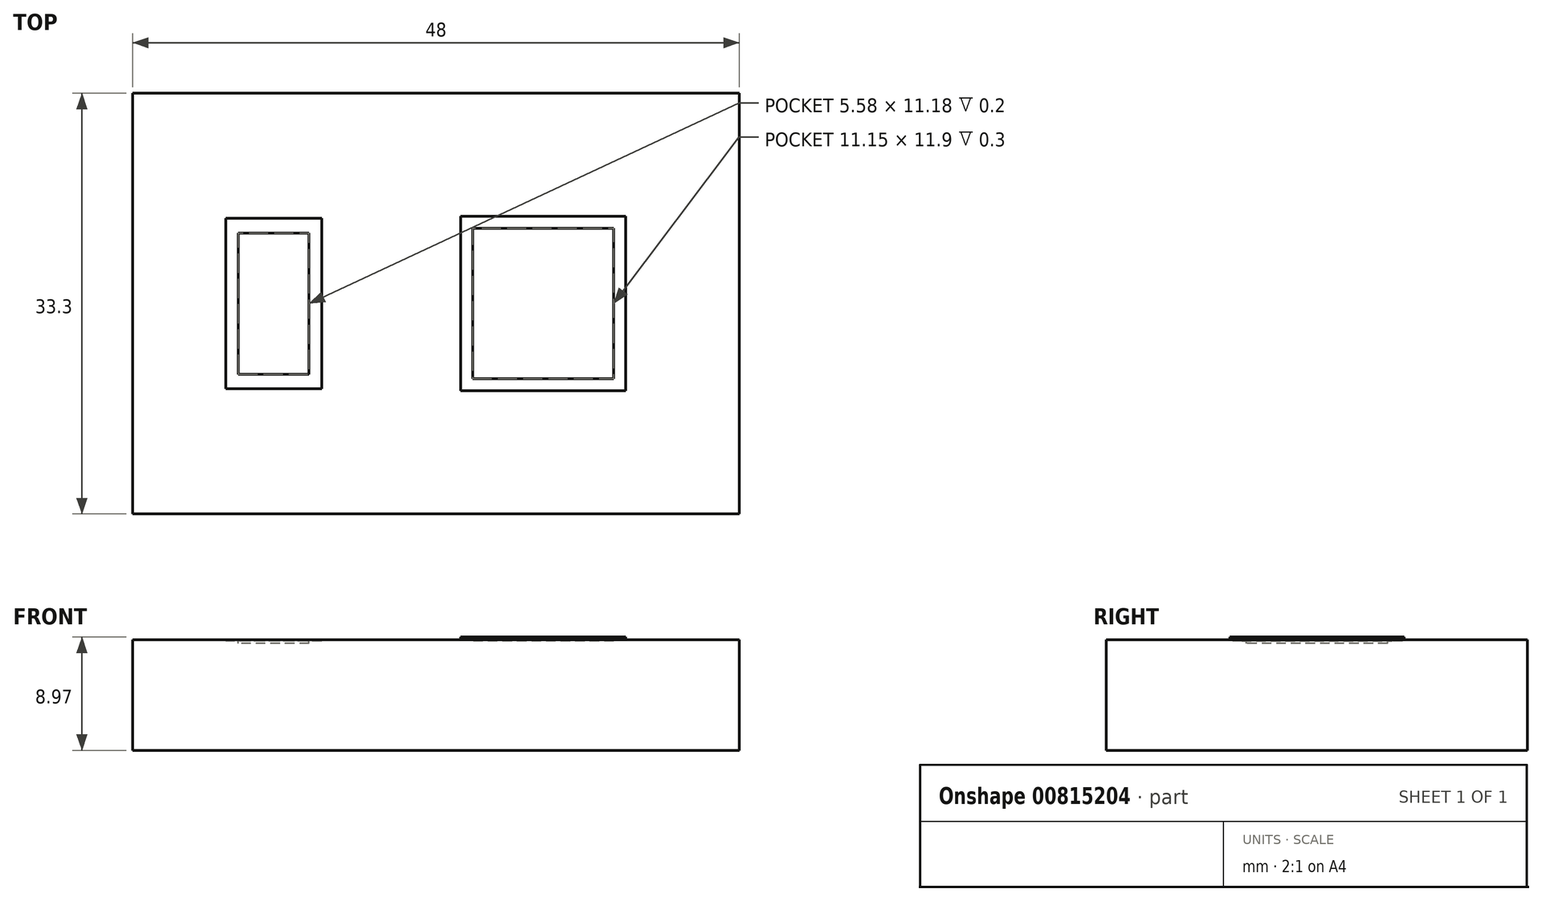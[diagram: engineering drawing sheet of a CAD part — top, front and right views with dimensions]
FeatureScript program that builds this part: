
annotation { "Feature Type Name" : "Feature", "Feature Type Description" : "" }
export const myFeature = defineFeature(function(context is Context, id is Id, definition is map)
    precondition{}
    {
        {
            var Q0;
            Q0=qCreatedBy(makeId("Top.planeOp"),FACE);
            var sketch = newSketch(context, id + "F0", { "sketchPlane" : qUnion([Q0])});
            skLineSegment(sketch, "E0.bottom", {"start": v(24, 16.65) * mm, "end": v(-24, 16.65) * mm});
            skLineSegment(sketch, "E0.top", {"start": v(24, -16.65) * mm, "end": v(-24, -16.65) * mm});
            skLineSegment(sketch, "E0.left", {"start": v(24, 16.65) * mm, "end": v(24, -16.65) * mm});
            skLineSegment(sketch, "E0.right", {"start": v(-24, 16.65) * mm, "end": v(-24, -16.65) * mm});
            skPoint(sketch, "E0.middle", {"position": v(0, 0) * mm});
            skSolve(sketch);
        }
        {
            var Q0;
            Q0 = qSketchRegion(id + "F0", true);
            extrude(context, id + "F1", {"entities" : qUnion([Q0]), "depth" : 8.77 * mm, "offsetDistance" : 25 * mm});
        }
        {
            var Q0;
            Q0=makeQuery(id+"F1.opExtrude","CAP_FACE",FACE,{"disambiguationData":[OSD([sQuery(id+"F0.wireOp",EDGE,"E0.bottom"),sQuery(id+"F0.wireOp",EDGE,"E0.top"),sQuery(id+"F0.wireOp",EDGE,"E0.left"),sQuery(id+"F0.wireOp",EDGE,"E0.right")])],"isStart":false});
            var sketch = newSketch(context, id + "F2", { "sketchPlane" : qUnion([Q0])});
            skLineSegment(sketch, "E1.bottom", {"start": v(-9.04, 6.75) * mm, "end": v(-16.64, 6.75) * mm});
            skLineSegment(sketch, "E1.top", {"start": v(-9.04, -6.75) * mm, "end": v(-16.64, -6.75) * mm});
            skLineSegment(sketch, "E1.left", {"start": v(-9.04, 6.75) * mm, "end": v(-9.04, -6.75) * mm});
            skLineSegment(sketch, "E1.right", {"start": v(-16.64, 6.75) * mm, "end": v(-16.64, -6.75) * mm});
            skPoint(sketch, "E1.middle", {"position": v(-12.84, 0) * mm});
            skLineSegment(sketch, "E2.bottom", {"start": v(-10.05, 5.6) * mm, "end": v(-15.63, 5.6) * mm});
            skLineSegment(sketch, "E2.top", {"start": v(-10.05, -5.6) * mm, "end": v(-15.63, -5.6) * mm});
            skLineSegment(sketch, "E2.left", {"start": v(-10.05, 5.6) * mm, "end": v(-10.05, -5.6) * mm});
            skLineSegment(sketch, "E2.right", {"start": v(-15.63, 5.6) * mm, "end": v(-15.63, -5.6) * mm});
            skSolve(sketch);
        }
        {
            var Q0;
            Q0 = qSketchRegion(id + "F2", true);
            extrude(context, id + "F3", {"entities" : qUnion([Q0]), "operationType" : NewBodyOperationType.REMOVE, "endBound" : BoundingType.SYMMETRIC, "oppositeDirection" : true, "depth" : .2 * mm, "offsetDistance" : 25 * mm});
        }
        {
            var Q0;
            Q0=makeQuery(id+"F3.boolean.opBoolean","SPLIT",FACE,{"disambiguationData":[TD([makeQuery(id+"F3.opExtrude","SWEPT_FACE",FACE,{"disambiguationData":[OSD([sQuery(id+"F2.wireOp",EDGE,"E2.bottom")])]})])],"derivedFrom":makeQuery(id+"F1.opExtrude","CAP_FACE",FACE,{"disambiguationData":[OSD([sQuery(id+"F0.wireOp",EDGE,"E0.bottom"),sQuery(id+"F0.wireOp",EDGE,"E0.top"),sQuery(id+"F0.wireOp",EDGE,"E0.left"),sQuery(id+"F0.wireOp",EDGE,"E0.right")])],"isStart":false})});
            extrude(context, id + "F4", {"entities" : qUnion([Q0]), "operationType" : NewBodyOperationType.REMOVE, "oppositeDirection" : true, "depth" : .3 * mm, "offsetDistance" : 25 * mm});
        }
        {
            var Q0;
            {var subQ0=sQuery(id+"F0.wireOp",EDGE,"E0.left");var subQ1=sQuery(id+"F0.wireOp",EDGE,"E0.top");var subQ2=sQuery(id+"F0.wireOp",EDGE,"E0.right");var subQ3=sQuery(id+"F0.wireOp",EDGE,"E0.bottom");Q0=makeQuery(id+"F3.boolean.opBoolean","SPLIT",FACE,{"disambiguationData":[TD([makeQuery(id+"F1.opExtrude","SWEPT_FACE",FACE,{"disambiguationData":[OSD([subQ3])]})])],"derivedFrom":makeQuery(id+"F1.opExtrude","CAP_FACE",FACE,{"disambiguationData":[OSD([subQ3,subQ1,subQ0,subQ2])],"isStart":false})});}
            var sketch = newSketch(context, id + "F5", { "sketchPlane" : qUnion([Q0])});
            skLineSegment(sketch, "E3.bottom", {"start": v(1.94, -6.9) * mm, "end": v(15.01, -6.9) * mm});
            skLineSegment(sketch, "E3.top", {"start": v(1.94, 6.9) * mm, "end": v(15.01, 6.9) * mm});
            skLineSegment(sketch, "E3.left", {"start": v(1.94, -6.9) * mm, "end": v(1.94, 6.9) * mm});
            skLineSegment(sketch, "E3.right", {"start": v(15.01, -6.9) * mm, "end": v(15.01, 6.9) * mm});
            skPoint(sketch, "E3.middle", {"position": v(8.48, 0) * mm});
            skLineSegment(sketch, "E4.bottom", {"start": v(14.05, -5.95) * mm, "end": v(2.9, -5.95) * mm});
            skLineSegment(sketch, "E4.top", {"start": v(14.05, 5.95) * mm, "end": v(2.9, 5.95) * mm});
            skLineSegment(sketch, "E4.left", {"start": v(14.05, -5.95) * mm, "end": v(14.05, 5.95) * mm});
            skLineSegment(sketch, "E4.right", {"start": v(2.9, -5.95) * mm, "end": v(2.9, 5.95) * mm});
            skSolve(sketch);
        }
        {
            var Q0;
            Q0 = qSketchRegion(id + "F5", true);
            extrude(context, id + "F6", {"entities" : qUnion([Q0]), "operationType" : NewBodyOperationType.ADD, "depth" : .2 * mm, "offsetDistance" : 25 * mm});
        }
        {
            var Q0;
            {var subQ0=sQuery(id+"F0.wireOp",EDGE,"E0.left");var subQ1=sQuery(id+"F0.wireOp",EDGE,"E0.top");var subQ2=sQuery(id+"F0.wireOp",EDGE,"E0.right");var subQ3=sQuery(id+"F0.wireOp",EDGE,"E0.bottom");Q0=makeQuery(id+"F6.boolean.opBoolean","SPLIT",FACE,{"disambiguationData":[TD([makeQuery(id+"F6.opExtrude","SWEPT_FACE",FACE,{"disambiguationData":[OSD([sQuery(id+"F5.wireOp",EDGE,"E4.bottom")])]})])],"derivedFrom":makeQuery(id+"F3.boolean.opBoolean","SPLIT",FACE,{"disambiguationData":[TD([makeQuery(id+"F1.opExtrude","SWEPT_FACE",FACE,{"disambiguationData":[OSD([subQ3])]})])],"derivedFrom":makeQuery(id+"F1.opExtrude","CAP_FACE",FACE,{"disambiguationData":[OSD([subQ3,subQ1,subQ0,subQ2])],"isStart":false})})});}
            extrude(context, id + "F7", {"entities" : qUnion([Q0]), "operationType" : NewBodyOperationType.REMOVE, "oppositeDirection" : true, "depth" : .1 * mm, "offsetDistance" : 25 * mm});
        }
    });
